# Revit family: Hekatron_Feststellanlagen_Ex-Anschlußdose_DE_22.01
name_source: partatom
category: Brandmelder
revit_build: Autodesk Revit 2018 (Build: 20190510_1515(x64)
units: mm (PartAtom-declared; Revit-internal decimal feet)

## family parameters
Basisbauteil = Fläche
Beim Laden mit Abzugskörper schneiden = Nein
Bemaßung runder Anschluss = Durchmesser verwenden
Beschriftungsausrichtung beibehalten = Ja
Gemeinsam genutzt = Nein
OmniClass-Nummer = 23.85.30.21
OmniClass-Titel = Environmental Detection/Registration
Raumberechnungspunkt = Nein
Teiletyp = Normal

## types (1)
- Ex-Junction Box
    Beschreibung = Anschlussdose mit dreipoliger Klemmleiste zur Installation in den Ex-Zonen 1,2 und 22 sowie im sicheren Bereich. Gemäß ATEX.
    Breite (mm) = 55.0
    Ex-Zonen = 1, 2, 21, 22
    Farbe = schwarz RAL 9005
    Hersteller = Hekatron
    Höhe (mm) = 80.0
    Kabeleinführung = oben, unten
    Link zu ausschreiben.de = http://www.ausschreiben.de
    Material = Polyester
    Modell = Ex-Anschlußdose
    Montageart = Aufputz
    Schutzart = IP 66/67
    Tiefe (mm) = 75.0
    Typenkommentare = Ex-Anschlussdose für Ex-Magnete Zone 1 und 2
    UB A&S Artikel Nummer = 6900360
    URL = https://www.hekatron-brandschutz.de
    Version des BIM Objektes = 22.01
    Vorgabe-Ansicht = 1200 mm

## geometry (parser evidence)
native form markers: Sweep x2
no freeform markers — native parametric forms only
